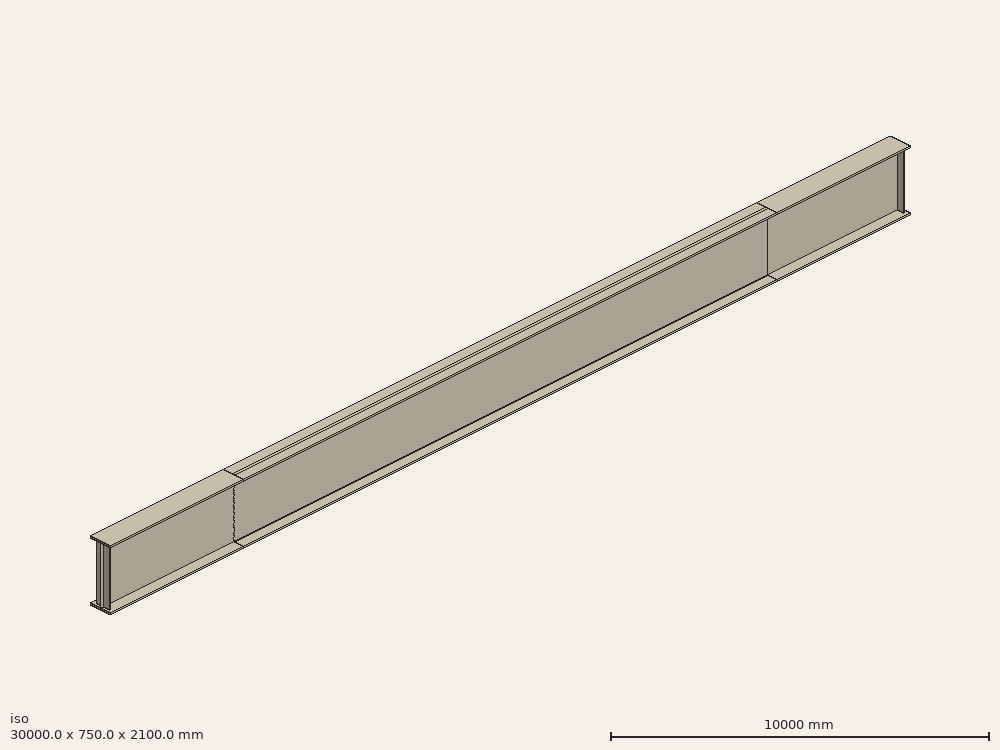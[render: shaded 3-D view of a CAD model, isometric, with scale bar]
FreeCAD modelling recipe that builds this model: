
FCSTD DOCUMENT  (FreeCAD 0.21R33771 (Git))
Label: train_bridge
License: All rights reserved
LicenseURL: http://en.wikipedia.org/wiki/All_rights_reserved
objects: Sketcher::SketchObject×4, Part::Extrusion×4, Part::FeaturePython×3, Fem::ConstraintForce×3, Fem::ConstraintDisplacement×2, Image::ImagePlane×1, Fem::FemMeshObjectPython×1, Fem::FemSolverObjectPython×1, App::MaterialObjectPython×1, Fem::FemAnalysis×1
note: 11 computed .brp shape members not serialized (recipe doc carries the construction recipe); baked Part::Feature solids carry a one-line shape summary decoded from their .brp

FEATURE [Sketcher::SketchObject] Sketch
  FullyConstrained = true
  Placement = pos=(0,0,0) rot=(0.57735,0.57735,0.57735;2.0944rad)
  sketch-geometry (12):
    g0: LineSegment StartX=-7.5 StartY=1000 StartZ=0 EndX=-7.5 EndY=-1000 EndZ=0
    g1: LineSegment StartX=-7.5 StartY=-1000 StartZ=0 EndX=-375 EndY=-1000 EndZ=0
    g2: LineSegment StartX=-375 StartY=-1000 StartZ=0 EndX=-375 EndY=-1050 EndZ=0
    g3: LineSegment StartX=-375 StartY=-1050 StartZ=0 EndX=375 EndY=-1050 EndZ=0
    g4: LineSegment StartX=375 StartY=-1050 StartZ=0 EndX=375 EndY=-1000 EndZ=0
    g5: LineSegment StartX=375 StartY=-1000 StartZ=0 EndX=7.5 EndY=-1000 EndZ=0
    g6: LineSegment StartX=7.5 StartY=-1000 StartZ=0 EndX=7.5 EndY=1000 EndZ=0
    g7: LineSegment StartX=7.5 StartY=1000 StartZ=0 EndX=375 EndY=1000 EndZ=0
    g8: LineSegment StartX=375 StartY=1000 StartZ=0 EndX=375 EndY=1050 EndZ=0
    g9: LineSegment StartX=375 StartY=1050 StartZ=0 EndX=-375 EndY=1050 EndZ=0
    g10: LineSegment StartX=-375 StartY=1050 StartZ=0 EndX=-375 EndY=1000 EndZ=0
    g11: LineSegment StartX=-375 StartY=1000 StartZ=0 EndX=-7.5 EndY=1000 EndZ=0
  constraints (32):
    c: Vertical(g0)
    c: Coincident(g0,g1)
    c: Horizontal(g1)
    c: Coincident(g1,g2)
    c: Vertical(g2)
    c: Coincident(g2,g3)
    c: Coincident(g3,g4)
    c: Vertical(g4)
    c: Coincident(g4,g5)
    c: Horizontal(g5)
    c: Coincident(g5,g6)
    c: Vertical(g6)
    c: Coincident(g6,g7)
    c: Horizontal(g7)
    c: Coincident(g7,g8)
    c: Vertical(g8)
    c: Coincident(g8,g9)
    c: Coincident(g9,g10)
    c: Coincident(g10,g11)
    c: Coincident(g11,g0)
    c: Horizontal(g11)
    c: Symmetric(g9,g8,g-2)
    c: Vertical(g10)
    c: DistanceX(g9,g9) = 750
    c: Symmetric(g2,g3,g-2)
    c: Symmetric(g0,g6,g-2)
    c: Symmetric(g8,g3,g-1)
    c: Equal(g8,g4)
    c: Horizontal(g0,g5)
    c: DistanceY(g8,g8) = 50
    c: DistanceX(g0,g5) = 15
    c: DistanceY(g3,g8) = 2100
FEATURE [Part::Extrusion] Extrude  label="part_left"
  Base = -> Sketch
  Dir = (1,0,0)
  DirMode = 0
  FaceMakerClass = Part::FaceMakerBullseye
  LengthFwd = 5000
  LengthRev = 0
  Solid = true
  Symmetric = false
FEATURE [Sketcher::SketchObject] Sketch001
  ExternalGeometry = -> [Extrude]
  FullyConstrained = true
  MapMode = 5
  Placement = pos=(5000,0,0) rot=(0.57735,0.57735,0.57735;2.0944rad)
  Support = -> [Extrude]
  sketch-geometry (12):
    g0: LineSegment StartX=-50 StartY=1050 StartZ=0 EndX=50 EndY=1050 EndZ=0
    g1: LineSegment StartX=50 StartY=1050 StartZ=0 EndX=50 EndY=1000 EndZ=0
    g2: LineSegment StartX=50 StartY=1000 StartZ=0 EndX=7.5 EndY=1000 EndZ=0
    g3: LineSegment StartX=7.5 StartY=1000 StartZ=0 EndX=7.5 EndY=-1000 EndZ=0
    g4: LineSegment StartX=7.5 StartY=-1000 StartZ=0 EndX=50 EndY=-1000 EndZ=0
    g5: LineSegment StartX=50 StartY=-1000 StartZ=0 EndX=50 EndY=-1050 EndZ=0
    g6: LineSegment StartX=50 StartY=-1050 StartZ=0 EndX=-50 EndY=-1050 EndZ=0
    g7: LineSegment StartX=-50 StartY=-1050 StartZ=0 EndX=-50 EndY=-1000 EndZ=0
    g8: LineSegment StartX=-50 StartY=-1000 StartZ=0 EndX=-7.5 EndY=-1000 EndZ=0
    g9: LineSegment StartX=-7.5 StartY=-1000 StartZ=0 EndX=-7.5 EndY=1000 EndZ=0
    g10: LineSegment StartX=-7.5 StartY=1000 StartZ=0 EndX=-50 EndY=1000 EndZ=0
    g11: LineSegment StartX=-50 StartY=1000 StartZ=0 EndX=-50 EndY=1050 EndZ=0
  constraints (31):
    c: Coincident(g0,g1)
    c: Vertical(g1)
    c: Coincident(g1,g2)
    c: Horizontal(g2)
    c: Coincident(g2,g3)
    c: Coincident(g3,g4)
    c: Horizontal(g4)
    c: Coincident(g4,g5)
    c: Vertical(g5)
    c: Coincident(g5,g6)
    c: Horizontal(g6)
    c: Coincident(g6,g7)
    c: Vertical(g7)
    c: Coincident(g7,g8)
    c: Coincident(g8,g9)
    c: Coincident(g9,g10)
    c: Horizontal(g10)
    c: Coincident(g11,g10)
    c: Coincident(g11,g0)
    c: Vertical(g11)
    c: Symmetric(g0,g0,g-2)
    c: Horizontal(g0,g-3)
    c: Coincident(g9,g-7)
    c: Coincident(g2,g-6)
    c: DistanceX(g0,g0) = 100
    c: Horizontal(g8)
    c: Coincident(g8,g-7)
    c: Coincident(g3,g-6)
    c: Horizontal(g5,g-4)
    c: Vertical(g1,g4)
    c: Vertical(g10,g7)
FEATURE [Part::Extrusion] Extrude001  label="web_middle"
  Base = -> Sketch001
  Dir = (1,0,0)
  DirMode = 0
  FaceMakerClass = Part::FaceMakerBullseye
  LengthFwd = 20000
  LengthRev = 0
  Solid = true
  Symmetric = false
FEATURE [Part::FeaturePython] Clone  label="part_right"  # Draft clone (typed FeaturePython)
  AttacherType = Attacher::AttachEngine3D
  Fuse = false
  Objects = -> [Extrude]
  Placement = pos=(25000,0,0) rot=(0,0,1;0rad)
  Scale = (1,1,1)
FEATURE [Sketcher::SketchObject] Sketch002
  ExternalGeometry = -> [Extrude001,Extrude]
  FullyConstrained = true
  MapMode = 5
  Placement = pos=(5000,0,0) rot=(0.57735,0.57735,0.57735;2.0944rad)
  Support = -> [Extrude]
  sketch-geometry (16):
    g0: LineSegment StartX=-375 StartY=1050 StartZ=0 EndX=-50 EndY=1050 EndZ=0
    g1: LineSegment StartX=-50 StartY=1050 StartZ=0 EndX=-50 EndY=1000 EndZ=0
    g2: LineSegment StartX=-50 StartY=1000 StartZ=0 EndX=-375 EndY=1000 EndZ=0
    g3: LineSegment StartX=-375 StartY=1000 StartZ=0 EndX=-375 EndY=1050 EndZ=0
    g4: LineSegment StartX=50 StartY=1050 StartZ=0 EndX=375 EndY=1050 EndZ=0
    g5: LineSegment StartX=375 StartY=1050 StartZ=0 EndX=375 EndY=1000 EndZ=0
    g6: LineSegment StartX=375 StartY=1000 StartZ=0 EndX=50 EndY=1000 EndZ=0
    g7: LineSegment StartX=50 StartY=1000 StartZ=0 EndX=50 EndY=1050 EndZ=0
    g8: LineSegment StartX=-375 StartY=-1000 StartZ=0 EndX=-50 EndY=-1000 EndZ=0
    g9: LineSegment StartX=-50 StartY=-1000 StartZ=0 EndX=-50 EndY=-1050 EndZ=0
    g10: LineSegment StartX=-50 StartY=-1050 StartZ=0 EndX=-375 EndY=-1050 EndZ=0
    g11: LineSegment StartX=-375 StartY=-1050 StartZ=0 EndX=-375 EndY=-1000 EndZ=0
    g12: LineSegment StartX=50 StartY=-1000 StartZ=0 EndX=375 EndY=-1000 EndZ=0
    g13: LineSegment StartX=375 StartY=-1000 StartZ=0 EndX=375 EndY=-1050 EndZ=0
    g14: LineSegment StartX=375 StartY=-1050 StartZ=0 EndX=50 EndY=-1050 EndZ=0
    g15: LineSegment StartX=50 StartY=-1050 StartZ=0 EndX=50 EndY=-1000 EndZ=0
  constraints (40):
    c: Coincident(g0,g1)
    c: Coincident(g1,g2)
    c: Coincident(g2,g3)
    c: Coincident(g3,g0)
    c: Horizontal(g0)
    c: Horizontal(g2)
    c: Vertical(g1)
    c: Vertical(g3)
    c: Coincident(g0,g-8)
    c: Coincident(g1,g-3)
    c: Coincident(g4,g5)
    c: Coincident(g5,g6)
    c: Coincident(g6,g7)
    c: Coincident(g7,g4)
    c: Horizontal(g4)
    c: Horizontal(g6)
    c: Vertical(g5)
    c: Vertical(g7)
    c: Coincident(g4,g-4)
    c: Coincident(g5,g-7)
    c: Coincident(g8,g9)
    c: Coincident(g9,g10)
    c: Coincident(g10,g11)
    c: Coincident(g11,g8)
    c: Horizontal(g8)
    c: Horizontal(g10)
    c: Vertical(g9)
    c: Vertical(g11)
    c: Coincident(g8,g-10)
    c: Coincident(g9,g-5)
    c: Coincident(g12,g13)
    c: Coincident(g13,g14)
    c: Coincident(g14,g15)
    c: Coincident(g15,g12)
    c: Horizontal(g12)
    c: Horizontal(g14)
    c: Vertical(g13)
    c: Vertical(g15)
    c: Coincident(g12,g-6)
    c: Coincident(g13,g-9)
FEATURE [Part::Extrusion] Extrude002  label="flanges_middle"
  Base = -> Sketch002
  Dir = (1,0,0)
  DirMode = 0
  FaceMakerClass = Part::FaceMakerBullseye
  LengthFwd = 20000
  LengthRev = 0
  Solid = true
  Symmetric = false
FEATURE [Image::ImagePlane] ImagePlane  label="steam_loco"
  Placement = pos=(15788,1000,2664) rot=(-1,0,0;4.71239rad)
  XSize = 26229.8
  YSize = 8852.3
  expr: XSize = 282.29 * 92.918 mm
  expr: YSize = 95.27 * 92.918 mm
FEATURE [Sketcher::SketchObject] Sketch003
  ExternalGeometry = -> [Extrude]
  FullyConstrained = true
  MapMode = 5
  Placement = pos=(0,0,0) rot=(0.57735,-0.57735,-0.57735;2.0944rad)
  Support = -> [Extrude]
  sketch-geometry (4):
    g0: LineSegment StartX=-250 StartY=1000 StartZ=0 EndX=250 EndY=1000 EndZ=0
    g1: LineSegment StartX=250 StartY=1000 StartZ=0 EndX=250 EndY=-1050 EndZ=0
    g2: LineSegment StartX=250 StartY=-1050 StartZ=0 EndX=-250 EndY=-1050 EndZ=0
    g3: LineSegment StartX=-250 StartY=-1050 StartZ=0 EndX=-250 EndY=1000 EndZ=0
  constraints (11):
    c: Coincident(g0,g1)
    c: Coincident(g1,g2)
    c: Coincident(g2,g3)
    c: Coincident(g3,g0)
    c: Horizontal(g2)
    c: Vertical(g1)
    c: Vertical(g3)
    c: Symmetric(g0,g0,g-2)
    c: Horizontal(g0,g-4)
    c: Horizontal(g2,g-5)
    c: DistanceX(g2,g2) = 500
FEATURE [Part::Extrusion] Extrude003  label="end_stiffener_right"
  Base = -> Sketch003
  Dir = (1,0,0)
  DirMode = 0
  FaceMakerClass = Part::FaceMakerBullseye
  LengthFwd = 20
  LengthRev = 0
  Placement = pos=(100,0,0) rot=(0,0,1;0rad)
  Solid = true
  Symmetric = false
FEATURE [Part::FeaturePython] Clone001  label="end_stiffener_left"  # Draft clone (typed FeaturePython)
  AttacherType = Attacher::AttachEngine3D
  Fuse = false
  Objects = -> [Extrude003]
  Placement = pos=(29880,0,0) rot=(0,0,1;0rad)
  Scale = (1,1,1)
  expr: .Placement.Base.x = 30000 - 120
FEATURE [Part::FeaturePython] BooleanFragments  label="girder1"  # WARN: FeaturePython — macro-defined, semantics opaque (R4)
  Mode = 0
  Objects = -> [Extrude,Extrude001,Clone,Extrude002,Extrude003,Clone001]
  Tolerance = 0
FEATURE [Fem::FemMeshObjectPython] FEMMeshGmsh  # FEM object (typed FeaturePython)
  Algorithm2D = 0
  Algorithm3D = 0
  CharacteristicLengthMax = 300
  CharacteristicLengthMin = 0
  CoherenceMesh = true
  ElementDimension = 3
  ElementOrder = 1
  GeometryTolerance = 1e-06
  GroupsOfNodes = false
  HighOrderOptimize = 0
  MeshSizeFromCurvature = 12
  OptimizeNetgen = false
  OptimizeStd = true
  Part = -> BooleanFragments
  RecombinationAlgorithm = 0
  Recombine3DAll = false
  RecombineAll = false
  SecondOrderLinear = false
FEATURE [Fem::FemSolverObjectPython] SolverCcxTools  # FEM object (typed FeaturePython)
  AnalysisType = 0
  BeamShellResultOutput3D = true
  BucklingFactors = 1
  EigenmodeHighLimit = 1000000
  EigenmodeLowLimit = 0
  EigenmodesCount = 10
  GeometricalNonlinearity = 0
  IterationsControlParameterCutb = 0.25,0.5,0.75,0.85,,,1.5,
  IterationsControlParameterIter = 4,8,9,200,10,400,,200,,
  IterationsControlParameterTimeUse = false
  IterationsThermoMechMaximum = 2000
  IterationsUserDefinedIncrementations = false
  IterationsUserDefinedTimeStepLength = false
  MaterialNonlinearity = 0
  MatrixSolverType = 0
  SplitInputWriter = true
  ThermoMechSteadyState = true
  TimeEnd = 1
  TimeInitialStep = 0.01
FEATURE [App::MaterialObjectPython] MaterialSolid  label="S235"  # material (typed FeaturePython)
  Category = 0
  Material = AuthorAndLicense=(c) 2013 Juergen Riegel (CC-BY 3.0),CardName=CalculiX-Steel,Density=7900 kg/m^3,+8 more (map truncated)
FEATURE [Fem::ConstraintDisplacement] ConstraintDisplacement  label="XYZ"
  NormalDirection = (0,0,1)
  Normals = (4) [(0,0,1),(0,0,1),(0,0,1),(0,0,1)]
  Points = (4) [(100,-250,-1050),(100,-83.3333,-1050),(100,83.3333,-1050),(100,250,-1050)]
  References = -> [BooleanFragments]
  Scale = 24
  hasXFormula = false
  hasYFormula = false
  hasZFormula = false
  rotxFix = false
  rotxFree = true
  rotyFix = false
  rotyFree = true
  rotzFix = false
  rotzFree = true
  useFlowSurfaceForce = false
  xDisplacement = 0
  xFix = true
  xFree = false
  xRotation = 0
  yDisplacement = 0
  yFix = true
  yFree = false
  yRotation = 0
  zDisplacement = 0
  zFix = true
  zFree = false
  zRotation = 0
FEATURE [Fem::ConstraintDisplacement] ConstraintDisplacement001  label="YZ"
  NormalDirection = (0,0,1)
  Normals = (4) [(0,0,1),(0,0,1),(0,0,1),(0,0,1)]
  Points = (4) [(29900,-250,-1050),(29900,-83.3333,-1050),(29900,83.3333,-1050),(29900,250,-1050)]
  References = -> [BooleanFragments]
  Scale = 24
  hasXFormula = false
  hasYFormula = false
  hasZFormula = false
  rotxFix = false
  rotxFree = true
  rotyFix = false
  rotyFree = true
  rotzFix = false
  rotzFree = true
  useFlowSurfaceForce = false
  xDisplacement = 0
  xFix = false
  xFree = true
  xRotation = 0
  yDisplacement = 0
  yFix = true
  yFree = false
  yRotation = 0
  zDisplacement = 0
  zFix = true
  zFree = false
  zRotation = 0
FEATURE [Fem::ConstraintForce] ConstraintForce  label="compensation_right"
  DirectionVector = (0,0,1)
  Force = 573500
  NormalDirection = (0,0,-1)
  Points = (12) [(29900,-250,-1050),(29900,-83.3333,-1050),(29900,83.3333,-1050),(29900,250,-1050),(29890,-250,-1050),(29890,-83.3333,-1050),(29890,83.3333,-1050),+5 more]
  References = -> [BooleanFragments]
  Reversed = true
  Scale = 17
FEATURE [Fem::ConstraintForce] ConstraintForce001  label="loco_load"
  DirectionVector = (0,0,-1)
  Force = 900000
  NormalDirection = (0,0,1)
  Points = (108) [(25000,-50,1050),(25000,-16.6667,1050),(25000,16.6667,1050),(25000,50,1050),(24230.8,-50,1050),(24230.8,-16.6667,1050),(24230.8,16.6667,1050),+101 more]
  References = -> [BooleanFragments]
  Reversed = true
  Scale = 78
FEATURE [Fem::ConstraintForce] ConstraintForce002  label="compensation_left"
  DirectionVector = (0,0,1)
  Force = 573500
  NormalDirection = (0,0,-1)
  Points = (12) [(120,-250,-1050),(120,-83.3333,-1050),(120,83.3333,-1050),(120,250,-1050),(110,-250,-1050),(110,-83.3333,-1050),(110,83.3333,-1050),(110,250,-1050),+4 more]
  References = -> [BooleanFragments]
  Reversed = true
  Scale = 17
FEATURE [Fem::FemAnalysis] Analysis
  Group = -> [SolverCcxTools,MaterialSolid,ConstraintDisplacement,ConstraintDisplacement001,FEMMeshGmsh,ConstraintForce,ConstraintForce001,ConstraintForce002]
